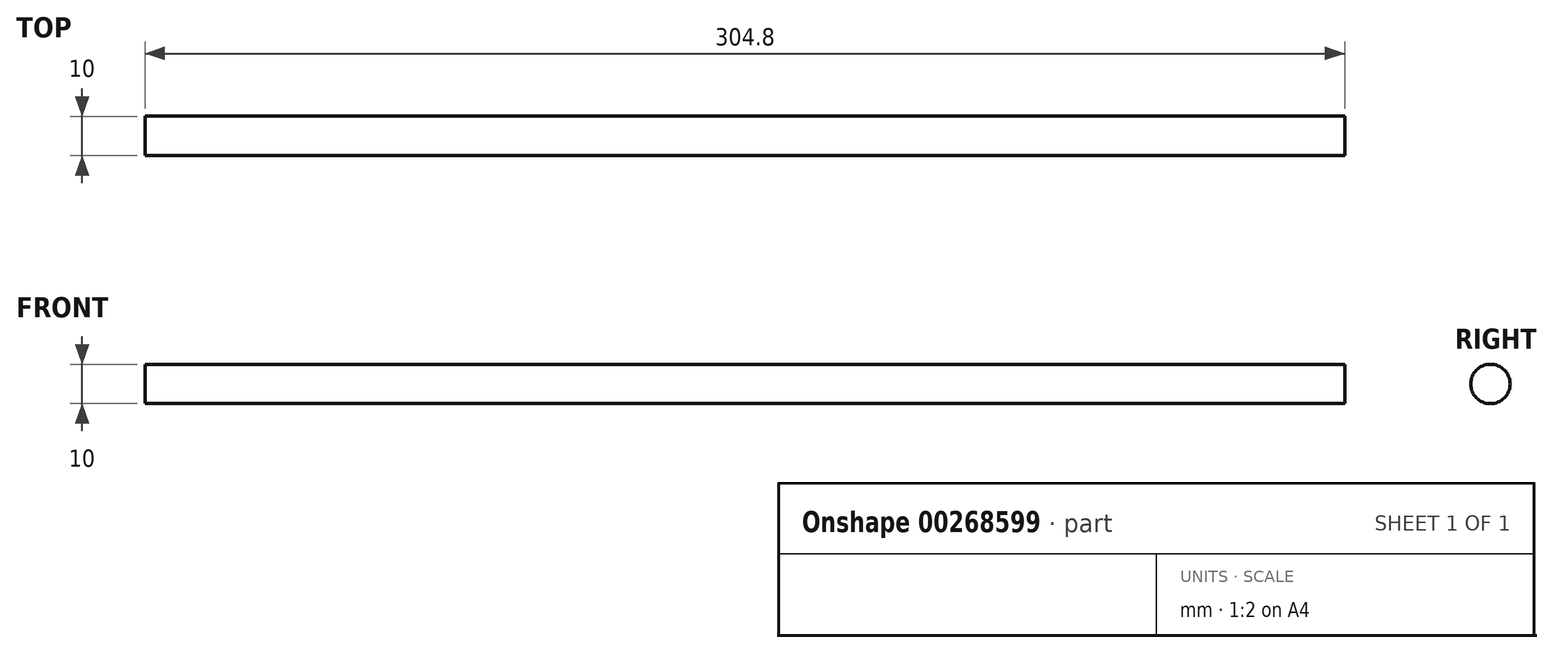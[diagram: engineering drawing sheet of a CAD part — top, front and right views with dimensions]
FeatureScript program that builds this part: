
annotation { "Feature Type Name" : "Feature", "Feature Type Description" : "" }
export const myFeature = defineFeature(function(context is Context, id is Id, definition is map)
    precondition{}
    {
        {
            var Q0;
            Q0=qCreatedBy(makeId("Right.planeOp"),FACE);
            var sketch = newSketch(context, id + "F0", { "sketchPlane" : qUnion([Q0])});
            skCircle(sketch, "E0", {"center": v(0, 0) * mm, "radius": 5 * mm});
            skSolve(sketch);
        }
        {
            var Q0;
            Q0=makeQuery(id+"F0.imprint","IMPRINT",FACE,{"disambiguationData":[TD([[makeQuery(id+"F0.imprint","IMPRINT",EDGE,{"derivedFrom":sQuery(id+"F0.wireOp",EDGE,"E0")}),1.0]])]});
            extrude(context, id + "F1", {"entities" : qUnion([Q0]), "depth" : 304.8 * mm, "offsetDistance" : 25.4 * mm});
        }
    });
